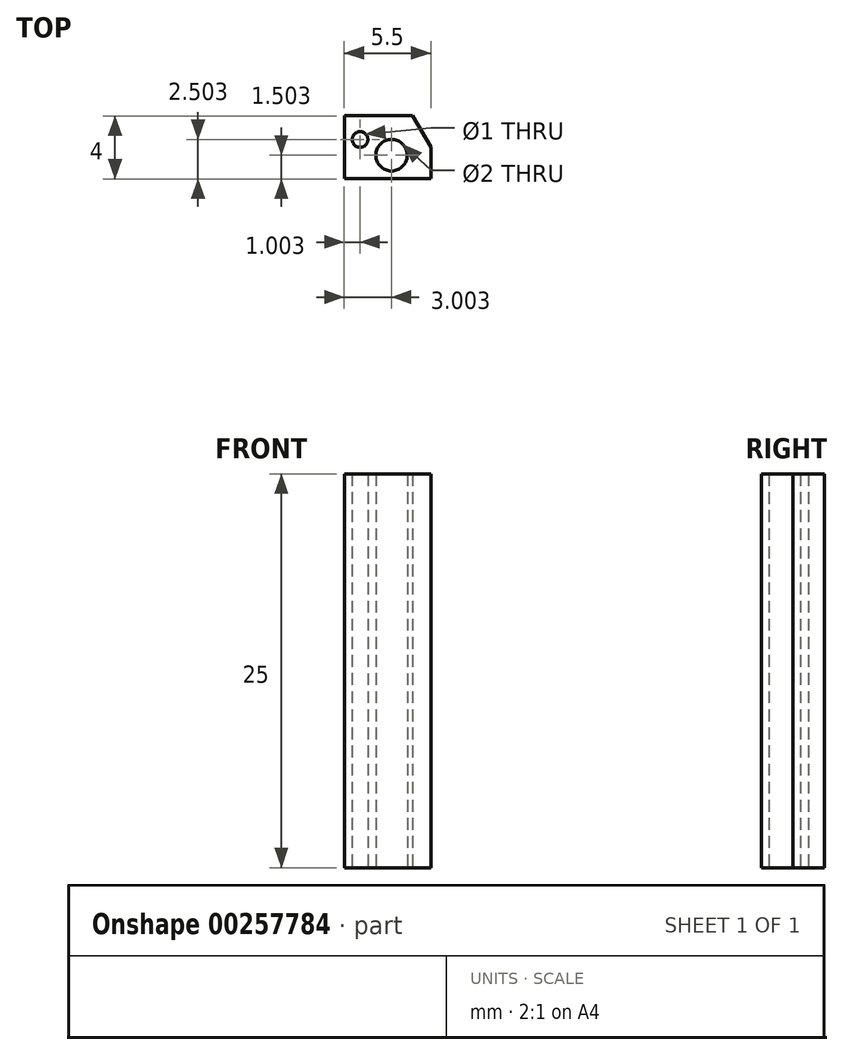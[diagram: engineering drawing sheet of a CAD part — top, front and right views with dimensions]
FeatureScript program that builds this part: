
annotation { "Feature Type Name" : "Feature", "Feature Type Description" : "" }
export const myFeature = defineFeature(function(context is Context, id is Id, definition is map)
    precondition{}
    {
        {
            var Q0;
            Q0=qCreatedBy(makeId("Top.planeOp"),FACE);
            var sketch = newSketch(context, id + "F0", { "sketchPlane" : qUnion([Q0])});
            skLineSegment(sketch, "E0", {"start": v(-11.1, 5.7) * mm, "end": v(-11.1, 1.7) * mm});
            skLineSegment(sketch, "E1", {"start": v(-11.1, 1.7) * mm, "end": v(-5.6, 1.7) * mm});
            skLineSegment(sketch, "E2", {"start": v(-5.6, 3.7) * mm, "end": v(-5.6, 1.7) * mm});
            skLineSegment(sketch, "E3", {"start": v(-11.1, 5.7) * mm, "end": v(-6.76, 5.7) * mm});
            skLineSegment(sketch, "E4", {"start": v(-5.6, 3.7) * mm, "end": v(-6.76, 5.7) * mm});
            skLineSegment(sketch, "E5", {"start": v(-11.1, 5.7) * mm, "end": v(-10.1, 5.7) * mm});
            skCircle(sketch, "E6", {"center": v(-10.1, 4.2) * mm, "radius": 0.5 * mm});
            skCircle(sketch, "E7", {"center": v(-8.1, 3.2) * mm, "radius": 0.5 * mm});
            skCircle(sketch, "E8", {"center": v(-8.1, 3.2) * mm, "radius": 1 * mm});
            skPoint(sketch, "E9.end.orphan", {"position": v(-8.1, 1.52) * mm});
            skPoint(sketch, "E9.start.orphan", {"position": v(-11.1, 1.52) * mm});
            skPoint(sketch, "E10.orphan", {"position": v(-8.1, 1.7) * mm});
            skSolve(sketch);
        }
        {
            var Q0;
            Q0 = qSketchRegion(id + "F0", true);
            extrude(context, id + "F1", {"entities" : qUnion([Q0]), "depth" : 25 * mm});
        }
        {
            var Q0;
            Q0 = qSketchRegion(id + "F0", true);
            extrude(context, id + "F2", {"entities" : qUnion([Q0]), "operationType" : NewBodyOperationType.ADD, "depth" : 25 * mm});
        }
    });
